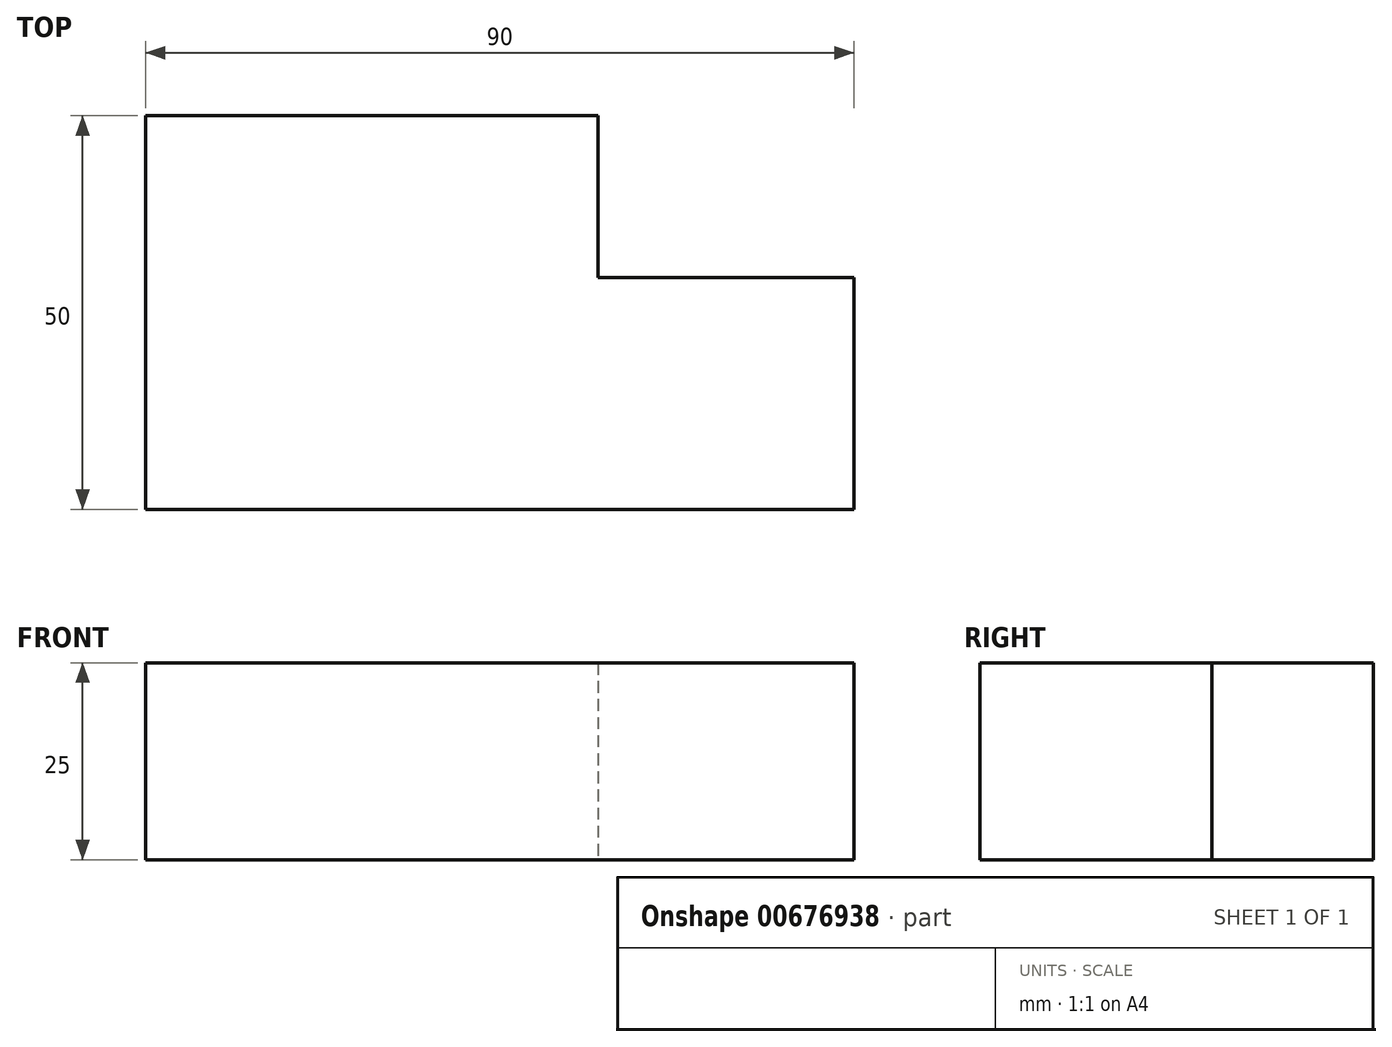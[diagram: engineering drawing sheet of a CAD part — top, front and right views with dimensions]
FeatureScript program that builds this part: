
annotation { "Feature Type Name" : "Feature", "Feature Type Description" : "" }
export const myFeature = defineFeature(function(context is Context, id is Id, definition is map)
    precondition{}
    {
        {
            var Q0;
            Q0=qCreatedBy(makeId("Top.planeOp"),FACE);
            var sketch = newSketch(context, id + "F0", { "sketchPlane" : qUnion([Q0])});
            skLineSegment(sketch, "E0.bottom", {"start": v(45, -25) * mm, "end": v(-45, -25) * mm});
            skLineSegment(sketch, "E0.top", {"start": v(45, 25) * mm, "end": v(-45, 25) * mm});
            skLineSegment(sketch, "E0.left", {"start": v(45, -25) * mm, "end": v(45, 25) * mm});
            skLineSegment(sketch, "E0.right", {"start": v(-45, -25) * mm, "end": v(-45, 25) * mm});
            skPoint(sketch, "E0.middle", {"position": v(0, 0) * mm});
            skLineSegment(sketch, "E1", {"start": v(12.48, 25) * mm, "end": v(12.48, 4.44) * mm});
            skLineSegment(sketch, "E2", {"start": v(12.48, 4.44) * mm, "end": v(45, 4.44) * mm});
            skSolve(sketch);
        }
        {
            var Q0;
            Q0 = qSketchRegion(id + "F0", true);
            extrude(context, id + "F1", {"entities" : qUnion([Q0]), "depth" : 25 * mm, "offsetDistance" : 25 * mm});
        }
        {
            var Q0;
            {var subQ3=sQuery(id+"F0.wireOp",EDGE,"E1");Q0=makeQuery(id+"F0.imprint","IMPRINT",FACE,{"disambiguationData":[TD([[makeQuery(id+"F0.imprint","IMPRINT",EDGE,{"derivedFrom":subQ3}),1.0]])]});}
            extrude(context, id + "F2", {"entities" : qUnion([Q0]), "operationType" : NewBodyOperationType.REMOVE, "depth" : 25 * mm, "offsetDistance" : 25 * mm});
        }
    });
